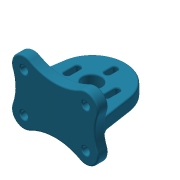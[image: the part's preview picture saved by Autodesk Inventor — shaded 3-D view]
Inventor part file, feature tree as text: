
AUTODESK INVENTOR PART (.ipt)
format: ipt  version: 2014 (Build 180170000, 170)  size: 568,832 bytes
history: native  units: mm
features: fillet x8, extrude x6, sketch x6, chamfer x1
ambient origin geometry x8: Origin, YZ Plane, XZ Plane, XY Plane, X Axis, Y Axis, Z Axis, Center Point
bodies: Solid1 (feature_tree)
feature tree (21):
  extrude  "Extrusion1"  Depth=41.0mm
  extrude  "Extrusion2"  Depth=6.0mm
  extrude  "Extrusion3"  Depth=35.0mm
  extrude  "Extrusion4"  Depth=22.0mm
  extrude  "Extrusion5"  Depth=50.0mm
  extrude  "Extrusion6"  Depth=0.5mm
  chamfer  "Chamfer1"  Distance=7.5mm
  fillet  "Fillet1"  Radius=3.6mm
  fillet  "Fillet2"  Radius=4.75mm
  fillet  "Fillet3"  Radius=2.5mm
  fillet  "Fillet4"  Radius=2.5mm
  fillet  "Fillet5"  Radius=13.0mm
  fillet  "Fillet6"  Radius=13.0mm
  fillet  "Fillet7"  Radius=7.0mm
  fillet  "Fillet8"  Radius=7.5mm
  sketch  "Sketch1"  dims[d0=26.0mm d1=41.0mm]
  sketch  "Sketch2"  dims[d2=4.5mm d3=6.0mm]
  sketch  "Sketch3"  dims[d4=30.0mm d5=35.0mm]
  sketch  "Sketch4"  dims[d6=7.0mm d7=0.0mm d8=22.0mm]
  sketch  "Sketch7"  dims[d9=18.0mm d10=50.0mm]
  sketch  "Sketch9"  dims[d11=8.5mm d12=0.0mm d13=12.0mm d14=7.5mm d15=0.0mm d16=3.6mm d17=4.75mm d18=2.5mm d19=2.5mm d20=13.0mm d21=13.0mm d22=7.0mm d23=7.5mm d24=0.0mm d25=5.75mm d26=3.5mm d27=0.0mm d28=10.5mm d29=2.0mm d30=0.0mm d31=3.0mm d32=2.0mm d33=45.0deg d34=1.0mm d35=0.75mm d36=1.0mm d37=1.0mm d38=1.0mm d39=1.0mm d40=0.5mm d41=0.5mm]
